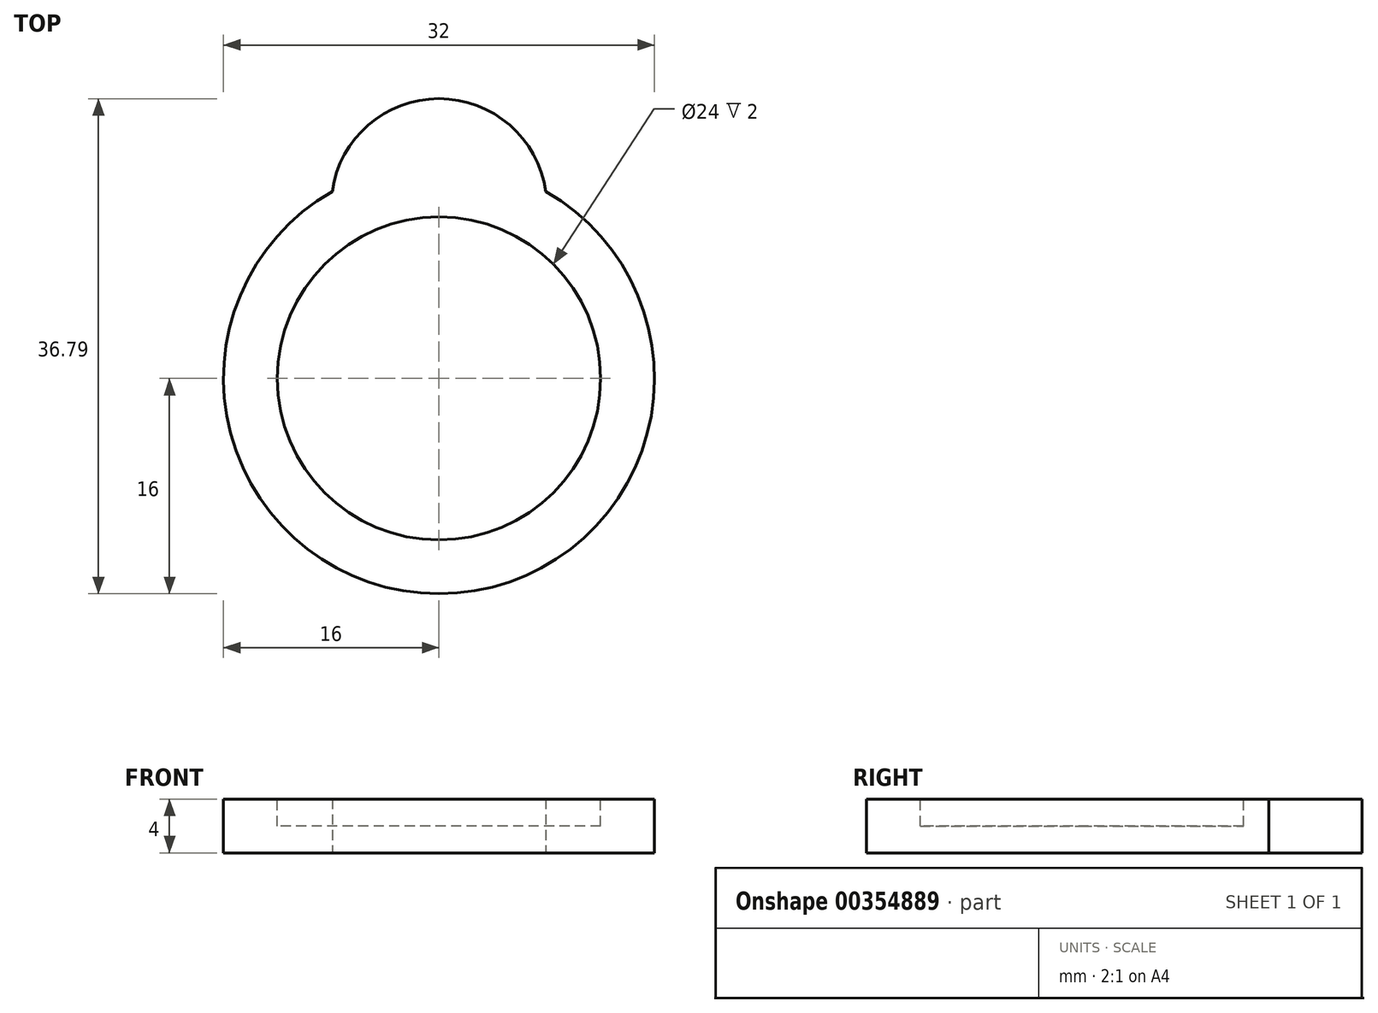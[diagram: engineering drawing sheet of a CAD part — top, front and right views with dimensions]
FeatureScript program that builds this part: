
annotation { "Feature Type Name" : "Feature", "Feature Type Description" : "" }
export const myFeature = defineFeature(function(context is Context, id is Id, definition is map)
    precondition{}
    {
        {
            var Q0;
            Q0=qCreatedBy(makeId("Top.planeOp"),FACE);
            var sketch = newSketch(context, id + "F0", { "sketchPlane" : qUnion([Q0])});
            skArc(sketch, "E0", {"start": v(-7.92, 13.9) * mm, "mid": v(0, -16) * mm, "end": v(7.92, 13.9) * mm});
            skArc(sketch, "E1", {"start": v(7.92, 13.9) * mm, "mid": v(0, 20.8) * mm, "end": v(-7.92, 13.9) * mm});
            skSolve(sketch);
        }
        {
            var Q0;
            Q0=makeQuery(id+"F0.imprint","IMPRINT",FACE,{"disambiguationData":[TD([[makeQuery(id+"F0.imprint","IMPRINT",EDGE,{"derivedFrom":sQuery(id+"F0.wireOp",EDGE,"E0")}),1.0]])]});
            extrude(context, id + "F1", {"entities" : qUnion([Q0]), "depth" : 4 * mm});
        }
        {
            var Q0;
            Q0=makeQuery(id+"F1.opExtrude","CAP_FACE",FACE,{"disambiguationData":[OSD([sQuery(id+"F0.wireOp",EDGE,"E0"),sQuery(id+"F0.wireOp",EDGE,"E1")])],"isStart":false});
            var sketch = newSketch(context, id + "F2", { "sketchPlane" : qUnion([Q0])});
            skCircle(sketch, "E2", {"center": v(0, 0) * mm, "radius": 12 * mm});
            skSolve(sketch);
        }
        {
            var Q0;
            Q0=makeQuery(id+"F2.imprint","IMPRINT",FACE,{"disambiguationData":[TD([[makeQuery(id+"F2.imprint","IMPRINT",EDGE,{"derivedFrom":sQuery(id+"F2.wireOp",EDGE,"E2")}),1.0]])]});
            var Q1;
            Q1=sQuery(id+"F2.wireOp",EDGE,"E2");
            extrude(context, id + "F3", {"entities" : qUnion([Q0]), "operationType" : NewBodyOperationType.REMOVE, "surfaceEntities" : qUnion([Q1]), "oppositeDirection" : true, "depth" : 2 * mm});
        }
    });
